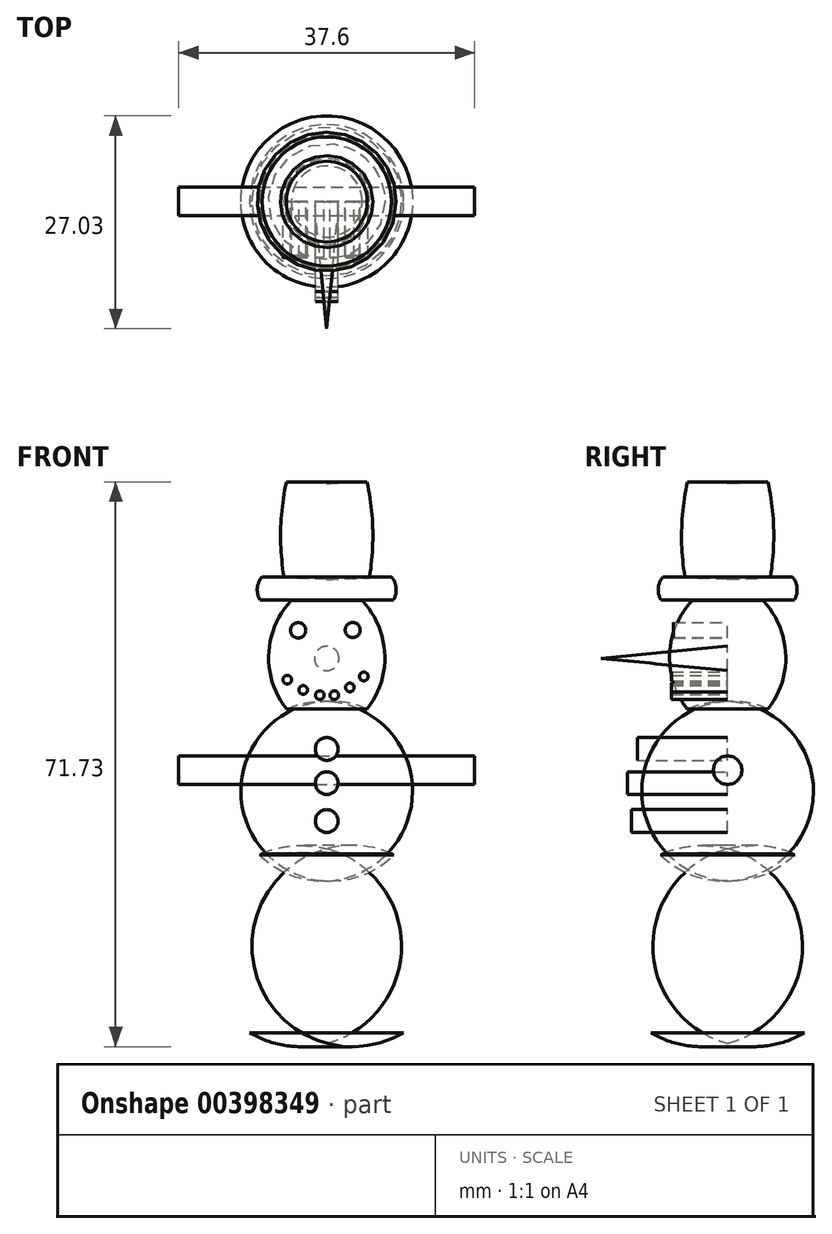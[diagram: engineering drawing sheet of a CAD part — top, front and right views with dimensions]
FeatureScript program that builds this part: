
annotation { "Feature Type Name" : "Feature", "Feature Type Description" : "" }
export const myFeature = defineFeature(function(context is Context, id is Id, definition is map)
    precondition{}
    {
        {
            var Q0;
            Q0=qCreatedBy(makeId("Front.planeOp"),FACE);
            var sketch = newSketch(context, id + "F0", { "sketchPlane" : qUnion([Q0])});
            skArc(sketch, "E0", {"start": v(17.07, -37.03) * mm, "mid": v(23.43, -16.72) * mm, "end": v(10.26, 0) * mm});
            skLineSegment(sketch, "E1", {"start": v(10.26, 0) * mm, "end": v(0, 0) * mm});
            skLineSegment(sketch, "E2", {"start": v(0, 0) * mm, "end": v(0, -37.03) * mm});
            skLineSegment(sketch, "E3", {"start": v(0, -37.03) * mm, "end": v(17.07, -37.03) * mm});
            skSolve(sketch);
        }
        {
            var Q0;
            Q0=makeQuery(id+"F0.imprint","IMPRINT",FACE,{"disambiguationData":[TD([[makeQuery(id+"F0.imprint","IMPRINT",EDGE,{"derivedFrom":sQuery(id+"F0.wireOp",EDGE,"E0")}),1.0]])]});
            var Q1;
            Q1=sQuery(id+"F0.wireOp",EDGE,"E2");
            revolve(context, id + "F1", {"entities" : qUnion([Q0]), "axis" : qUnion([Q1]), "revolveType" : RevolveType.FULL});
        }
        {
            var Q0;
            Q0=qCreatedBy(makeId("Front.planeOp"),FACE);
            var sketch = newSketch(context, id + "F2", { "sketchPlane" : qUnion([Q0])});
            skArc(sketch, "E4", {"start": v(19.56, -82.2) * mm, "mid": v(32.06, -58.58) * mm, "end": v(16.65, -36.73) * mm});
            skLineSegment(sketch, "E5", {"start": v(16.65, -36.73) * mm, "end": v(0, -36.4) * mm});
            skLineSegment(sketch, "E6", {"start": v(0, -36.4) * mm, "end": v(0, -82.2) * mm});
            skLineSegment(sketch, "E7", {"start": v(0, -82.2) * mm, "end": v(19.56, -82.2) * mm});
            skSolve(sketch);
        }
        {
            var Q0;
            Q0 = qSketchRegion(id + "F2", true);
            var Q1;
            Q1=sQuery(id+"F2.wireOp",EDGE,"goJ8fcNA-TH0V-PSOE-eMkZ-18O3zIWGTxwR");
            var Q2;
            Q2=sQuery(id+"F2.wireOp",EDGE,"E6");
            revolve(context, id + "F3", {"entities" : qUnion([Q0]), "surfaceEntities" : qUnion([Q1]), "axis" : qUnion([Q2]), "revolveType" : RevolveType.FULL});
        }
        {
            var Q0;
            Q0=qCreatedBy(makeId("Front.planeOp"),FACE);
            var sketch = newSketch(context, id + "F4", { "sketchPlane" : qUnion([Q0])});
            skArc(sketch, "E8", {"start": v(10.26, 0) * mm, "mid": v(14.74, 14.01) * mm, "end": v(9.03, 27.57) * mm});
            skLineSegment(sketch, "E9", {"start": v(9.03, 27.57) * mm, "end": v(0, 27.57) * mm});
            skLineSegment(sketch, "E10", {"start": v(0, 27.57) * mm, "end": v(0, 0) * mm});
            skLineSegment(sketch, "E11", {"start": v(0, 0) * mm, "end": v(10.26, 0) * mm});
            skSolve(sketch);
        }
        {
            var Q0;
            Q0 = qSketchRegion(id + "F4", true);
            var Q1;
            Q1=sQuery(id+"F4.wireOp",EDGE,"E10");
            revolve(context, id + "F5", {"entities" : qUnion([Q0]), "axis" : qUnion([Q1]), "revolveType" : RevolveType.FULL});
        }
        {
            var Q0;
            Q0=qCreatedBy(makeId("Front.planeOp"),FACE);
            var sketch = newSketch(context, id + "F6", { "sketchPlane" : qUnion([Q0])});
            skArc(sketch, "E12", {"start": v(16.93, 27.78) * mm, "mid": v(17.64, 30.78) * mm, "end": v(16.42, 33.6) * mm});
            skLineSegment(sketch, "E13", {"start": v(16.42, 33.6) * mm, "end": v(0, 32.92) * mm});
            skLineSegment(sketch, "E14", {"start": v(0, 32.92) * mm, "end": v(0, 27.78) * mm});
            skLineSegment(sketch, "E15", {"start": v(0, 27.78) * mm, "end": v(16.93, 27.78) * mm});
            skPoint(sketch, "E16", {"position": v(0, 30.35) * mm});
            skSolve(sketch);
        }
        {
            var Q0;
            Q0 = qSketchRegion(id + "F6", true);
            var Q1;
            Q1=sQuery(id+"F6.wireOp",EDGE,"E14");
            revolve(context, id + "F7", {"operationType" : NewBodyOperationType.ADD, "entities" : qUnion([Q0]), "axis" : qUnion([Q1]), "revolveType" : RevolveType.FULL});
        }
        {
            var Q0;
            Q0=qCreatedBy(makeId("Front.planeOp"),FACE);
            var sketch = newSketch(context, id + "F8", { "sketchPlane" : qUnion([Q0])});
            skArc(sketch, "E17", {"start": v(10.88, 33.61) * mm, "mid": v(11.7, 45.69) * mm, "end": v(10.25, 57.7) * mm});
            skLineSegment(sketch, "E18", {"start": v(10.25, 57.7) * mm, "end": v(0, 57.35) * mm});
            skLineSegment(sketch, "E19", {"start": v(0, 57.35) * mm, "end": v(0, 33.61) * mm});
            skLineSegment(sketch, "E20", {"start": v(0, 33.61) * mm, "end": v(10.88, 33.61) * mm});
            skSolve(sketch);
        }
        {
            var Q0;
            Q0 = qSketchRegion(id + "F8", true);
            var Q1;
            Q1=sQuery(id+"F8.wireOp",EDGE,"E19");
            revolve(context, id + "F9", {"entities" : qUnion([Q0]), "axis" : qUnion([Q1]), "revolveType" : RevolveType.FULL});
        }
        {
            var Q0;
            Q0=qCreatedBy(makeId("Front.planeOp"),FACE);
            var sketch = newSketch(context, id + "F10", { "sketchPlane" : qUnion([Q0])});
            skCircle(sketch, "E21", {"center": v(0, -10.13) * mm, "radius": 2.9 * mm});
            skSolve(sketch);
        }
        {
            var Q0;
            Q0 = qSketchRegion(id + "F10", true);
            extrude(context, id + "F11", {"entities" : qUnion([Q0]), "depth" : 22.86 * mm});
        }
        {
            var Q0;
            Q0=qCreatedBy(makeId("Front.planeOp"),FACE);
            var sketch = newSketch(context, id + "F12", { "sketchPlane" : qUnion([Q0])});
            skCircle(sketch, "E22", {"center": v(0, -18.8) * mm, "radius": 2.9 * mm});
            skSolve(sketch);
        }
        {
            var Q0;
            Q0 = qSketchRegion(id + "F12", true);
            extrude(context, id + "F13", {"entities" : qUnion([Q0]), "depth" : 25.4 * mm});
        }
        {
            var Q0;
            Q0=qCreatedBy(makeId("Front.planeOp"),FACE);
            var sketch = newSketch(context, id + "F14", { "sketchPlane" : qUnion([Q0])});
            skCircle(sketch, "E23", {"center": v(0, -28.45) * mm, "radius": 2.9 * mm});
            skSolve(sketch);
        }
        {
            var Q0;
            Q0 = qSketchRegion(id + "F14", true);
            extrude(context, id + "F15", {"entities" : qUnion([Q0]), "depth" : 24.38 * mm});
        }
        {
            var Q0;
            Q0=qCreatedBy(makeId("Front.planeOp"),FACE);
            var sketch = newSketch(context, id + "F16", { "sketchPlane" : qUnion([Q0])});
            skCircle(sketch, "E24", {"center": v(6.6, 20.1) * mm, "radius": 1.92 * mm});
            skCircle(sketch, "E25", {"center": v(-7.27, 20.02) * mm, "radius": 1.95 * mm});
            skSolve(sketch);
        }
        {
            var Q0;
            Q0 = qSketchRegion(id + "F16", true);
            extrude(context, id + "F17", {"entities" : qUnion([Q0]), "depth" : 13.72 * mm});
        }
        {
            var Q0;
            Q0=qCreatedBy(makeId("Front.planeOp"),FACE);
            var sketch = newSketch(context, id + "F18", { "sketchPlane" : qUnion([Q0])});
            skCircle(sketch, "E26", {"center": v(-10.01, 7.48) * mm, "radius": 1.1 * mm});
            skCircle(sketch, "E27", {"center": v(-5.99, 4.87) * mm, "radius": 1.1 * mm});
            skCircle(sketch, "E28", {"center": v(-1.77, 3.54) * mm, "radius": 1.1 * mm});
            skCircle(sketch, "E29", {"center": v(1.95, 3.55) * mm, "radius": 1.1 * mm});
            skCircle(sketch, "E30", {"center": v(9.41, 8.3) * mm, "radius": 1.1 * mm});
            skCircle(sketch, "E31", {"center": v(5.88, 5.52) * mm, "radius": 1.1 * mm});
            skSolve(sketch);
        }
        {
            var Q0;
            Q0 = qSketchRegion(id + "F18", true);
            extrude(context, id + "F19", {"entities" : qUnion([Q0]), "depth" : 14.22 * mm});
        }
        {
            var Q0;
            Q0=qCreatedBy(makeId("Front.planeOp"),FACE);
            var sketch = newSketch(context, id + "F20", { "sketchPlane" : qUnion([Q0])});
            skCircle(sketch, "E32", {"center": v(0, 12.88) * mm, "radius": 3.1 * mm});
            skSolve(sketch);
        }
        {
            var Q0;
            Q0 = qSketchRegion(id + "F20", true);
            extrude(context, id + "F21", {"entities" : qUnion([Q0]), "depth" : 32.77 * mm, "hasDraft" : true, "draftAngle" : 5.5 * degree, "draftPullDirection" : true});
        }
        {
            var Q0;
            Q0=qCreatedBy(makeId("Right.planeOp"),FACE);
            var sketch = newSketch(context, id + "F22", { "sketchPlane" : qUnion([Q0])});
            skCircle(sketch, "E33", {"center": v(0, -15.52) * mm, "radius": 3.61 * mm});
            skSolve(sketch);
        }
        {
            var Q0;
            Q0 = qSketchRegion(id + "F22", true);
            extrude(context, id + "F23", {"entities" : qUnion([Q0]), "endBound" : BoundingType.SYMMETRIC, "oppositeDirection" : true, "depth" : 75.18 * mm});
        }
        {
            var Q0;
            Q0=makeQuery(id+"F17.opExtrude","SWEPT_BODY",BODY,{"disambiguationData":[OSD([sQuery(id+"F16.wireOp",EDGE,"E25")])]});
            var Q1;
            Q1=makeQuery(id+"F19.opExtrude","SWEPT_BODY",BODY,{"disambiguationData":[OSD([sQuery(id+"F18.wireOp",EDGE,"E26")])]});
            var Q2;
            Q2=makeQuery(id+"F19.opExtrude","SWEPT_BODY",BODY,{"disambiguationData":[OSD([sQuery(id+"F18.wireOp",EDGE,"E27")])]});
            var Q3;
            Q3=makeQuery(id+"F19.opExtrude","SWEPT_BODY",BODY,{"disambiguationData":[OSD([sQuery(id+"F18.wireOp",EDGE,"E30")])]});
            var Q4;
            Q4=makeQuery(id+"F19.opExtrude","SWEPT_BODY",BODY,{"disambiguationData":[OSD([sQuery(id+"F18.wireOp",EDGE,"E31")])]});
            var Q5;
            Q5=makeQuery(id+"F1.opRevolve","SWEPT_BODY",BODY,{"disambiguationData":[OSD([sQuery(id+"F0.wireOp",EDGE,"E0"),sQuery(id+"F0.wireOp",EDGE,"E1"),sQuery(id+"F0.wireOp",EDGE,"E2"),sQuery(id+"F0.wireOp",EDGE,"E3")])]});
            var Q6;
            Q6=makeQuery(id+"F3.opRevolve","SWEPT_BODY",BODY,{"disambiguationData":[OSD([sQuery(id+"F2.wireOp",EDGE,"E4"),sQuery(id+"F2.wireOp",EDGE,"E5"),sQuery(id+"F2.wireOp",EDGE,"E6"),sQuery(id+"F2.wireOp",EDGE,"E7")])]});
            var Q7;
            Q7=makeQuery(id+"F5.opRevolve","SWEPT_BODY",BODY,{"disambiguationData":[OSD([sQuery(id+"F4.wireOp",EDGE,"E8"),sQuery(id+"F4.wireOp",EDGE,"E9"),sQuery(id+"F4.wireOp",EDGE,"E10"),sQuery(id+"F4.wireOp",EDGE,"E11")])]});
            var Q8;
            Q8=makeQuery(id+"F7.opRevolve","SWEPT_BODY",BODY,{"disambiguationData":[OSD([sQuery(id+"F6.wireOp",EDGE,"E12"),sQuery(id+"F6.wireOp",EDGE,"E13"),sQuery(id+"F6.wireOp",EDGE,"E14"),sQuery(id+"F6.wireOp",EDGE,"E15")])]});
            var Q9;
            Q9=makeQuery(id+"F9.opRevolve","SWEPT_BODY",BODY,{"disambiguationData":[OSD([sQuery(id+"F8.wireOp",EDGE,"E17"),sQuery(id+"F8.wireOp",EDGE,"E18"),sQuery(id+"F8.wireOp",EDGE,"E19"),sQuery(id+"F8.wireOp",EDGE,"E20")])]});
            var Q10;
            Q10=makeQuery(id+"F11.opExtrude","SWEPT_BODY",BODY,{"disambiguationData":[OSD([sQuery(id+"F10.wireOp",EDGE,"E21")])]});
            var Q11;
            Q11=makeQuery(id+"F13.opExtrude","SWEPT_BODY",BODY,{"disambiguationData":[OSD([sQuery(id+"F12.wireOp",EDGE,"E22")])]});
            var Q12;
            Q12=makeQuery(id+"F15.opExtrude","SWEPT_BODY",BODY,{"disambiguationData":[OSD([sQuery(id+"F14.wireOp",EDGE,"E23")])]});
            var Q13;
            Q13=makeQuery(id+"F17.opExtrude","SWEPT_BODY",BODY,{"disambiguationData":[OSD([sQuery(id+"F16.wireOp",EDGE,"E24")])]});
            var Q14;
            Q14=makeQuery(id+"F23.opExtrude","SWEPT_BODY",BODY,{"disambiguationData":[OSD([sQuery(id+"F22.wireOp",EDGE,"E33")])]});
            var Q15;
            Q15=makeQuery(id+"F19.opExtrude","SWEPT_BODY",BODY,{"disambiguationData":[OSD([sQuery(id+"F18.wireOp",EDGE,"E28")])]});
            var Q16;
            Q16=makeQuery(id+"F19.opExtrude","SWEPT_BODY",BODY,{"disambiguationData":[OSD([sQuery(id+"F18.wireOp",EDGE,"E29")])]});
            var Q17;
            Q17=makeQuery(id+"F21.opExtrude","SWEPT_BODY",BODY,{"disambiguationData":[OSD([sQuery(id+"F20.wireOp",EDGE,"E32")])]});
            var Q18;
            Q18=qCreatedBy(makeId("Origin.pointOp"),VERTEX);
            transform(context, id + "F24", {"entities" : qUnion([Q0, Q1, Q2, Q3, Q4, Q5, Q6, Q7, Q8, Q9, Q10, Q11, Q12, Q13, Q14, Q15, Q16, Q17]), "transformType" : TransformType.SCALE_UNIFORMLY, "scale" : .5, "scalePoint" : qUnion([Q18]), "makeCopy" : false});
        }
    });
